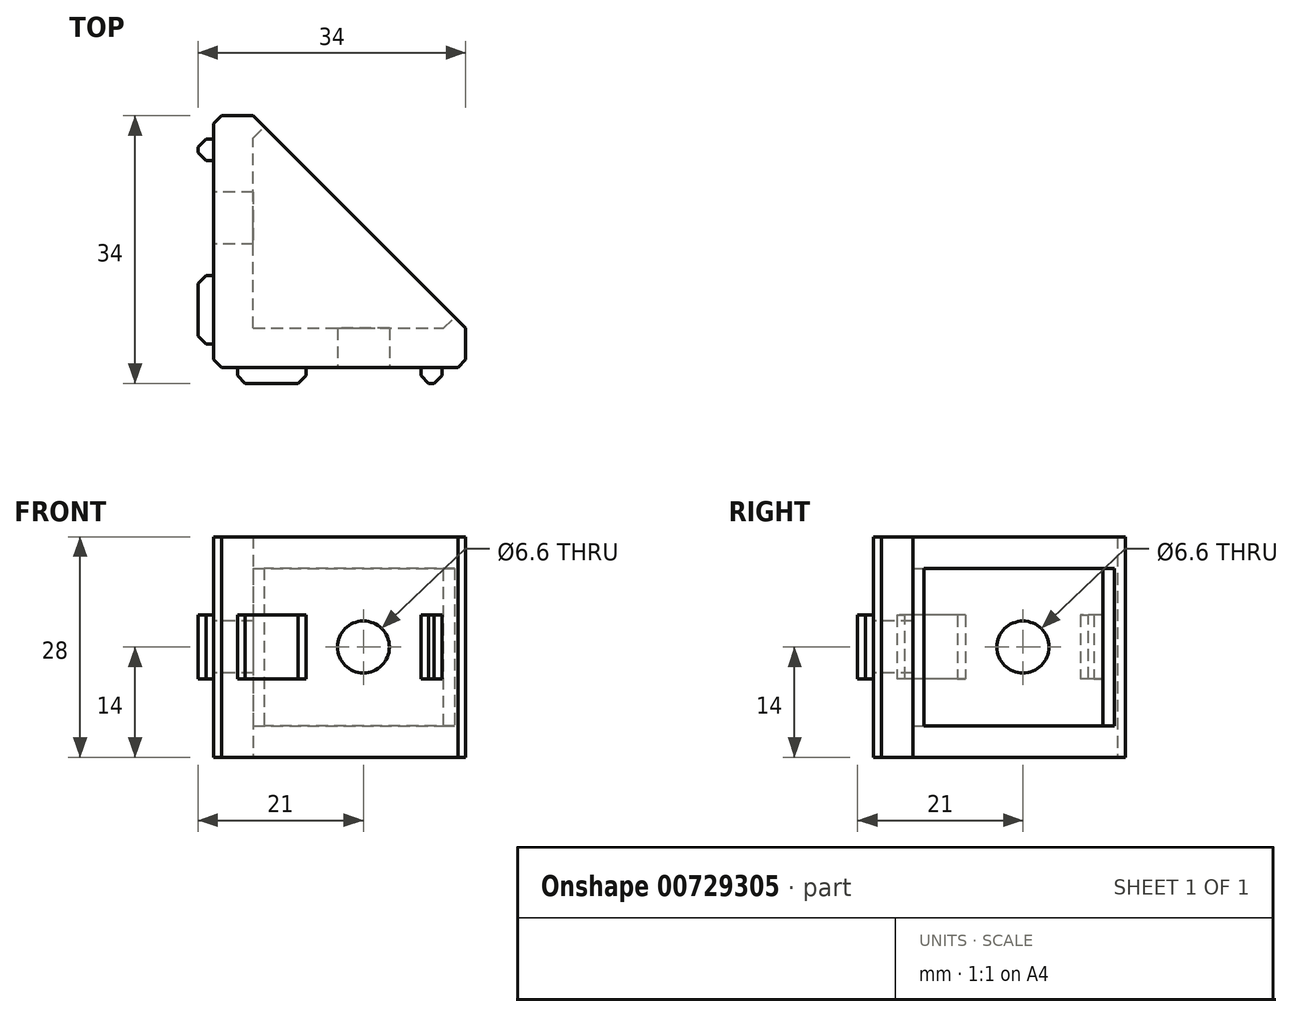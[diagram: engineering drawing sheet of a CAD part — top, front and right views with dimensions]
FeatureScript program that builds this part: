
annotation { "Feature Type Name" : "Feature", "Feature Type Description" : "" }
export const myFeature = defineFeature(function(context is Context, id is Id, definition is map)
    precondition{}
    {
        {
            var Q0;
            Q0=qCreatedBy(makeId("Top.planeOp"),FACE);
            var sketch = newSketch(context, id + "F0", { "sketchPlane" : qUnion([Q0])});
            skLineSegment(sketch, "E0", {"start": v(0, 0) * mm, "end": v(0, 32) * mm});
            skLineSegment(sketch, "E1", {"start": v(0, 32) * mm, "end": v(5, 32) * mm});
            skLineSegment(sketch, "E2", {"start": v(5, 32) * mm, "end": v(32, 5) * mm});
            skLineSegment(sketch, "E3", {"start": v(32, 5) * mm, "end": v(32, 0) * mm});
            skLineSegment(sketch, "E4", {"start": v(32, 0) * mm, "end": v(0, 0) * mm});
            skSolve(sketch);
        }
        {
            var Q0;
            Q0 = qSketchRegion(id + "F0", true);
            extrude(context, id + "F1", {"entities" : qUnion([Q0]), "depth" : 28 * mm, "offsetDistance" : 25 * mm});
        }
        {
            var Q0;
            Q0=makeQuery(id+"F1.opExtrude","SWEPT_FACE",FACE,{"disambiguationData":[OSD([sQuery(id+"F0.wireOp",EDGE,"E3")])]});
            var sketch = newSketch(context, id + "F2", { "sketchPlane" : qUnion([Q0])});
            skLineSegment(sketch, "E5.bottom", {"start": v(5, 24) * mm, "end": v(32, 24) * mm});
            skLineSegment(sketch, "E5.top", {"start": v(5, 4) * mm, "end": v(32, 4) * mm});
            skLineSegment(sketch, "E5.left", {"start": v(5, 24) * mm, "end": v(5, 4) * mm});
            skLineSegment(sketch, "E5.right", {"start": v(32, 24) * mm, "end": v(32, 4) * mm});
            skSolve(sketch);
        }
        {
            var Q0;
            Q0=makeQuery(id+"F2.imprint","IMPRINT",FACE,{"disambiguationData":[TD([[makeQuery(id+"F2.imprint","IMPRINT",EDGE,{"derivedFrom":sQuery(id+"F2.wireOp",EDGE,"E5.bottom")}),-1.0]])]});
            var Q1;
            Q1=makeQuery(id+"F1.opExtrude","CAP_VERTEX",VERTEX,{"disambiguationData":[OSD([sQuery(id+"F0.wireOp",EDGE,"E1"),sQuery(id+"F0.wireOp",EDGE,"E2")])],"isStart":true});
            extrude(context, id + "F3", {"entities" : qUnion([Q0]), "operationType" : NewBodyOperationType.REMOVE, "endBound" : BoundingType.UP_TO_VERTEX, "oppositeDirection" : true, "depth" : 25 * mm, "endBoundEntityVertex" : qUnion([Q1]), "offsetDistance" : 25 * mm});
        }
        {
            var Q0;
            Q0=makeQuery(id+"F3.boolean.opBoolean","COPY",FACE,{"derivedFrom":makeQuery(id+"F3.opExtrude","CAP_FACE",FACE,{"disambiguationData":[OSD([sQuery(id+"F2.wireOp",EDGE,"E5.bottom"),sQuery(id+"F2.wireOp",EDGE,"E5.top"),sQuery(id+"F2.wireOp",EDGE,"E5.left"),sQuery(id+"F2.wireOp",EDGE,"E5.right")])],"isStart":false})});
            var sketch = newSketch(context, id + "F4", { "sketchPlane" : qUnion([Q0])});
            skPoint(sketch, "E6", {"position": v(19, 14) * mm});
            skCircle(sketch, "E7", {"center": v(19, 14) * mm, "radius": 9 * mm, "construction": true});
            skSolve(sketch);
        }
        {
            var Q0;
            Q0=sQuery(id+"F4.wireOp",VERTEX,"E6");
            var Q1;
            Q1=makeQuery(id+"F1.opExtrude","SWEPT_BODY",BODY,{"disambiguationData":[OSD([sQuery(id+"F0.wireOp",EDGE,"E0"),sQuery(id+"F0.wireOp",EDGE,"E1"),sQuery(id+"F0.wireOp",EDGE,"E2"),sQuery(id+"F0.wireOp",EDGE,"E3"),sQuery(id+"F0.wireOp",EDGE,"E4")])]});
            hole(context, id + "F5", {"style" : HoleStyle.SIMPLE, "endStyle" : HoleEndStyle.THROUGH, "standardTappedOrClearance" : lookupTablePath({ "fit" : "Normal", "standard" : "ISO", "size" : "M6", "type" : "Clearance" }), "standardBlindInLast" : lookupTablePath({ "fit" : "Standard", "standard" : "ISO", "size" : "M6", "type" : "Clearance" }), "holeDiameter" : 6.6 * mm, "majorDiameter" : 5 * mm, "isTappedThrough" : true, "tappedDepth" : 12 * mm, "tapClearance" : 3, "locations" : qUnion([Q0]), "scope" : qUnion([Q1])});
        }
        {
            var Q0;
            Q0=makeQuery(id+"F3.boolean.opBoolean","COPY",FACE,{"derivedFrom":makeQuery(id+"F3.opExtrude","SWEPT_FACE",FACE,{"disambiguationData":[OSD([sQuery(id+"F2.wireOp",EDGE,"E5.left")])]})});
            var sketch = newSketch(context, id + "F6", { "sketchPlane" : qUnion([Q0])});
            skPoint(sketch, "E8", {"position": v(-19, 14) * mm});
            skSolve(sketch);
        }
        {
            var Q0;
            Q0=sQuery(id+"F6.wireOp",VERTEX,"E8");
            var Q1;
            Q1=makeQuery(id+"F1.opExtrude","SWEPT_BODY",BODY,{"disambiguationData":[OSD([sQuery(id+"F0.wireOp",EDGE,"E0"),sQuery(id+"F0.wireOp",EDGE,"E1"),sQuery(id+"F0.wireOp",EDGE,"E2"),sQuery(id+"F0.wireOp",EDGE,"E3"),sQuery(id+"F0.wireOp",EDGE,"E4")])]});
            hole(context, id + "F7", {"style" : HoleStyle.SIMPLE, "endStyle" : HoleEndStyle.THROUGH, "standardTappedOrClearance" : lookupTablePath({ "fit" : "Normal", "standard" : "ISO", "size" : "M6", "type" : "Clearance" }), "standardBlindInLast" : lookupTablePath({ "fit" : "Standard", "standard" : "ISO", "size" : "M6", "type" : "Clearance" }), "holeDiameter" : 6.6 * mm, "majorDiameter" : 5 * mm, "isTappedThrough" : true, "tappedDepth" : 12 * mm, "tapClearance" : 3, "locations" : qUnion([Q0]), "scope" : qUnion([Q1])});
        }
        {
            var Q0;
            Q0=makeQuery(id+"F1.opExtrude","SWEPT_FACE",FACE,{"disambiguationData":[OSD([sQuery(id+"F0.wireOp",EDGE,"E4")])]});
            var sketch = newSketch(context, id + "F8", { "sketchPlane" : qUnion([Q0])});
            skLineSegment(sketch, "E9.bottom", {"start": v(3, 18.05) * mm, "end": v(11.7, 18.05) * mm});
            skLineSegment(sketch, "E9.top", {"start": v(3, 9.95) * mm, "end": v(11.7, 9.95) * mm});
            skLineSegment(sketch, "E9.left", {"start": v(3, 18.05) * mm, "end": v(3, 9.95) * mm});
            skLineSegment(sketch, "E9.right", {"start": v(11.7, 18.05) * mm, "end": v(11.7, 9.95) * mm});
            skLineSegment(sketch, "E10.bottom", {"start": v(26.3, 18.05) * mm, "end": v(29, 18.05) * mm});
            skLineSegment(sketch, "E10.top", {"start": v(26.3, 9.95) * mm, "end": v(29, 9.95) * mm});
            skLineSegment(sketch, "E10.left", {"start": v(26.3, 18.05) * mm, "end": v(26.3, 9.95) * mm});
            skLineSegment(sketch, "E10.right", {"start": v(29, 18.05) * mm, "end": v(29, 9.95) * mm});
            skPoint(sketch, "E11", {"position": v(11.7, 14) * mm});
            skPoint(sketch, "E12", {"position": v(26.3, 14) * mm});
            skPoint(sketch, "E13", {"position": v(19, 14) * mm});
            skSolve(sketch);
        }
        {
            var Q0;
            Q0=makeQuery(id+"F8.imprint","IMPRINT",FACE,{"disambiguationData":[TD([[makeQuery(id+"F8.imprint","IMPRINT",EDGE,{"derivedFrom":sQuery(id+"F8.wireOp",EDGE,"E10.bottom")}),-1.0]])]});
            var Q1;
            Q1=makeQuery(id+"F8.imprint","IMPRINT",FACE,{"disambiguationData":[TD([[makeQuery(id+"F8.imprint","IMPRINT",EDGE,{"derivedFrom":sQuery(id+"F8.wireOp",EDGE,"E9.bottom")}),-1.0]])]});
            extrude(context, id + "F9", {"entities" : qUnion([Q0, Q1]), "operationType" : NewBodyOperationType.ADD, "depth" : 2 * mm, "offsetDistance" : 25 * mm});
        }
        {
            var Q0;
            Q0=makeQuery(id+"F1.opExtrude","SWEPT_FACE",FACE,{"disambiguationData":[OSD([sQuery(id+"F0.wireOp",EDGE,"E0")])]});
            var sketch = newSketch(context, id + "F10", { "sketchPlane" : qUnion([Q0])});
            skLineSegment(sketch, "E14.bottom", {"start": v(-29, 18.05) * mm, "end": v(-26.3, 18.05) * mm});
            skLineSegment(sketch, "E14.top", {"start": v(-29, 9.95) * mm, "end": v(-26.3, 9.95) * mm});
            skLineSegment(sketch, "E14.left", {"start": v(-29, 18.05) * mm, "end": v(-29, 9.95) * mm});
            skLineSegment(sketch, "E14.right", {"start": v(-26.3, 18.05) * mm, "end": v(-26.3, 9.95) * mm});
            skLineSegment(sketch, "E15.bottom", {"start": v(-11.7, 18.05) * mm, "end": v(-3, 18.05) * mm});
            skLineSegment(sketch, "E15.top", {"start": v(-11.7, 9.95) * mm, "end": v(-3, 9.95) * mm});
            skLineSegment(sketch, "E15.left", {"start": v(-11.7, 18.05) * mm, "end": v(-11.7, 9.95) * mm});
            skLineSegment(sketch, "E15.right", {"start": v(-3, 18.05) * mm, "end": v(-3, 9.95) * mm});
            skPoint(sketch, "E16", {"position": v(-26.3, 14) * mm});
            skPoint(sketch, "E17", {"position": v(-19, 14) * mm});
            skPoint(sketch, "E18", {"position": v(-11.7, 14) * mm});
            skSolve(sketch);
        }
        {
            var Q0;
            Q0=makeQuery(id+"F10.imprint","IMPRINT",FACE,{"disambiguationData":[TD([[makeQuery(id+"F10.imprint","IMPRINT",EDGE,{"derivedFrom":sQuery(id+"F10.wireOp",EDGE,"E14.bottom")}),-1.0]])]});
            var Q1;
            Q1=makeQuery(id+"F10.imprint","IMPRINT",FACE,{"disambiguationData":[TD([[makeQuery(id+"F10.imprint","IMPRINT",EDGE,{"derivedFrom":sQuery(id+"F10.wireOp",EDGE,"E15.bottom")}),-1.0]])]});
            extrude(context, id + "F11", {"entities" : qUnion([Q0, Q1]), "operationType" : NewBodyOperationType.ADD, "depth" : 2 * mm, "offsetDistance" : 25 * mm});
        }
        {
            var Q0;
            Q0=makeQuery(id+"F1.opExtrude","SWEPT_EDGE",EDGE,{"disambiguationData":[OSD([sQuery(id+"F0.wireOp",EDGE,"E0"),sQuery(id+"F0.wireOp",EDGE,"E1")])]});
            var Q1;
            Q1=makeQuery(id+"F11.opExtrude","CAP_EDGE",EDGE,{"disambiguationData":[OSD([sQuery(id+"F10.wireOp",EDGE,"E14.left")])],"isStart":false});
            var Q2;
            Q2=makeQuery(id+"F11.opExtrude","CAP_EDGE",EDGE,{"disambiguationData":[OSD([sQuery(id+"F10.wireOp",EDGE,"E14.right")])],"isStart":false});
            var Q3;
            Q3=makeQuery(id+"F11.opExtrude","CAP_EDGE",EDGE,{"disambiguationData":[OSD([sQuery(id+"F10.wireOp",EDGE,"E15.left")])],"isStart":false});
            var Q4;
            Q4=makeQuery(id+"F11.opExtrude","CAP_EDGE",EDGE,{"disambiguationData":[OSD([sQuery(id+"F10.wireOp",EDGE,"E15.right")])],"isStart":false});
            var Q5;
            Q5=makeQuery(id+"F1.opExtrude","SWEPT_EDGE",EDGE,{"disambiguationData":[OSD([sQuery(id+"F0.wireOp",EDGE,"E0"),sQuery(id+"F0.wireOp",EDGE,"E4")])]});
            var Q6;
            Q6=makeQuery(id+"F9.opExtrude","CAP_EDGE",EDGE,{"disambiguationData":[OSD([sQuery(id+"F8.wireOp",EDGE,"E9.left")])],"isStart":false});
            var Q7;
            Q7=makeQuery(id+"F9.opExtrude","CAP_EDGE",EDGE,{"disambiguationData":[OSD([sQuery(id+"F8.wireOp",EDGE,"E9.right")])],"isStart":false});
            var Q8;
            Q8=makeQuery(id+"F9.opExtrude","CAP_EDGE",EDGE,{"disambiguationData":[OSD([sQuery(id+"F8.wireOp",EDGE,"E10.left")])],"isStart":false});
            var Q9;
            Q9=makeQuery(id+"F9.opExtrude","CAP_EDGE",EDGE,{"disambiguationData":[OSD([sQuery(id+"F8.wireOp",EDGE,"E10.right")])],"isStart":false});
            var Q10;
            Q10=makeQuery(id+"F1.opExtrude","SWEPT_EDGE",EDGE,{"disambiguationData":[OSD([sQuery(id+"F0.wireOp",EDGE,"E3"),sQuery(id+"F0.wireOp",EDGE,"E4")])]});
            chamfer(context, id + "F12", {"entities" : qUnion([Q0, Q1, Q2, Q3, Q4, Q5, Q6, Q7, Q8, Q9, Q10]), "width" : 1 * mm, "tangentPropagation" : true});
        }
        {
            var Q0;
            {var subQ0=sQuery(id+"F2.wireOp",EDGE,"E5.bottom");var subQ3=sQuery(id+"F0.wireOp",EDGE,"E2");Q0=makeQuery(id+"F3.boolean.opBoolean","SPLIT",FACE,{"disambiguationData":[TD([makeQuery(id+"F3.opExtrude","SWEPT_FACE",FACE,{"disambiguationData":[OSD([subQ0])]})])],"derivedFrom":makeQuery(id+"F1.opExtrude","SWEPT_FACE",FACE,{"disambiguationData":[OSD([subQ3])]})});}
            var sketch = newSketch(context, id + "F13", { "sketchPlane" : qUnion([Q0])});
            skLineSegment(sketch, "E19.bottom", {"start": v(-19.1, 24) * mm, "end": v(-17.1, 24) * mm});
            skLineSegment(sketch, "E19.top", {"start": v(-19.1, 4) * mm, "end": v(-17.1, 4) * mm});
            skLineSegment(sketch, "E19.left", {"start": v(-19.1, 24) * mm, "end": v(-19.1, 4) * mm});
            skLineSegment(sketch, "E19.right", {"start": v(-17.1, 24) * mm, "end": v(-17.1, 4) * mm});
            skLineSegment(sketch, "E20.bottom", {"start": v(19.1, 24) * mm, "end": v(17.1, 24) * mm});
            skLineSegment(sketch, "E20.top", {"start": v(19.1, 4) * mm, "end": v(17.1, 4) * mm});
            skLineSegment(sketch, "E20.left", {"start": v(19.1, 24) * mm, "end": v(19.1, 4) * mm});
            skLineSegment(sketch, "E20.right", {"start": v(17.1, 24) * mm, "end": v(17.1, 4) * mm});
            skSolve(sketch);
        }
        {
            var Q0;
            Q0 = qSketchRegion(id + "F13", true);
            extrude(context, id + "F14", {"entities" : qUnion([Q0]), "operationType" : NewBodyOperationType.ADD, "oppositeDirection" : true, "depth" : 2.5 * mm, "offsetDistance" : 25 * mm});
        }
    });
